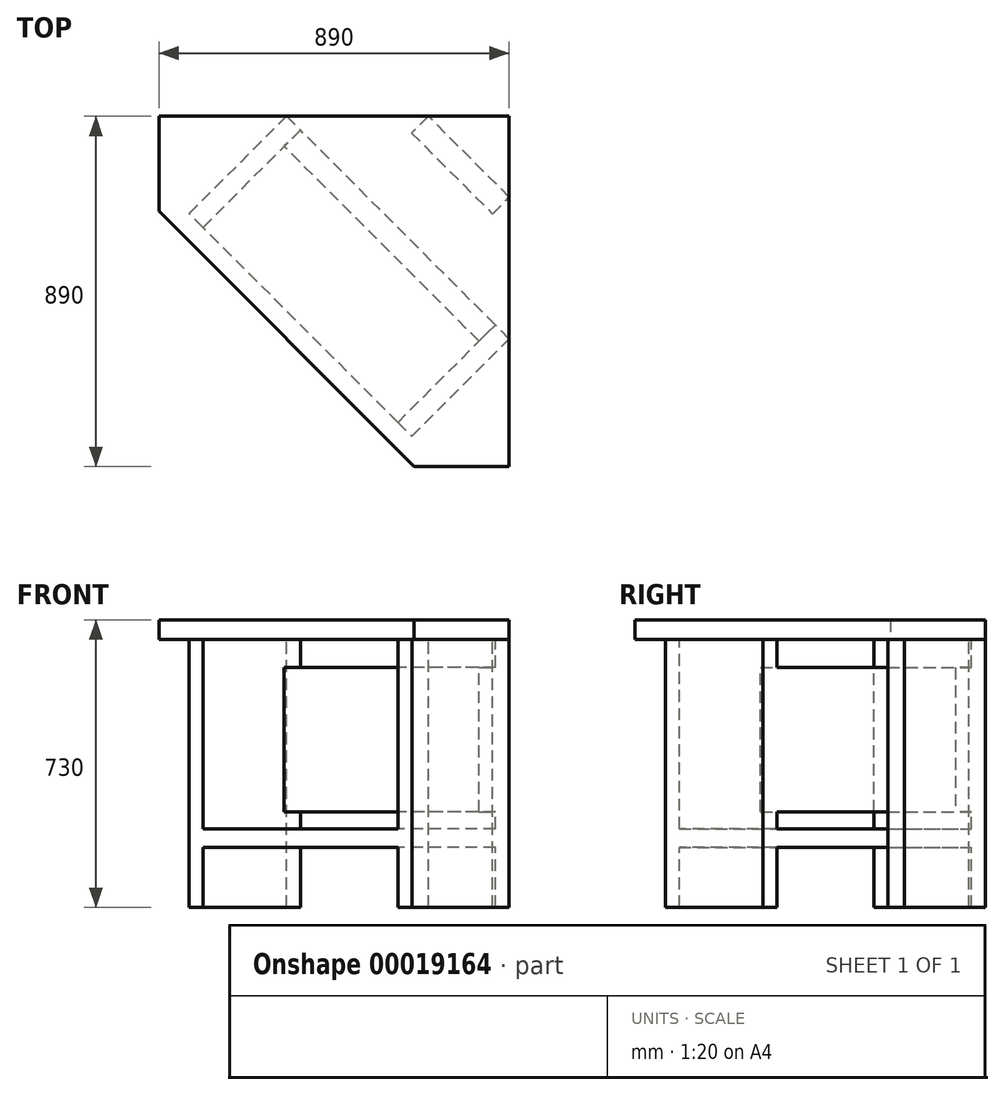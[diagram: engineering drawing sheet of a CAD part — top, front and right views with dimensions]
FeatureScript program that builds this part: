
annotation { "Feature Type Name" : "Feature", "Feature Type Description" : "" }
export const myFeature = defineFeature(function(context is Context, id is Id, definition is map)
    precondition{}
    {
        {
            var Q0;
            Q0=qCreatedBy(makeId("Top.planeOp"),FACE);
            var sketch = newSketch(context, id + "F0", { "sketchPlane" : qUnion([Q0])});
            skLineSegment(sketch, "E0", {"start": v(-890, 0) * mm, "end": v(0, 0) * mm});
            skLineSegment(sketch, "E1", {"start": v(0, 0) * mm, "end": v(0, -890) * mm});
            skLineSegment(sketch, "E2", {"start": v(0, -890) * mm, "end": v(-241.37, -890) * mm});
            skLineSegment(sketch, "E3", {"start": v(-241.37, -890) * mm, "end": v(-890, -241.37) * mm});
            skLineSegment(sketch, "E4", {"start": v(-890, -241.37) * mm, "end": v(-890, 0) * mm});
            skLineSegment(sketch, "E5", {"start": v(0, 0) * mm, "end": v(-565.69, -565.69) * mm, "construction": true});
            skSolve(sketch);
        }
        {
            var Q0;
            Q0=makeQuery(id+"F0.imprint","IMPRINT",FACE,{"disambiguationData":[TD([[makeQuery(id+"F0.imprint","IMPRINT",EDGE,{"derivedFrom":sQuery(id+"F0.wireOp",EDGE,"E0")}),-1.0]])]});
            extrude(context, id + "F1", {"entities" : qUnion([Q0]), "depth" : 50 * mm});
        }
        {
            var Q0;
            Q0=qCreatedBy(makeId("Right.planeOp"),FACE);
            var Q1;
            Q1=qCreatedBy(makeId("Front.planeOp"),FACE);
            cPlane(context, id + "F2", {"entities" : qUnion([Q0, Q1]), "cplaneType" : CPlaneType.MID_PLANE, "offset" : 150 * mm, "flipAlignment" : true, "width" : 150 * mm, "height" : 150 * mm});
        }
        {
            var Q0;
            Q0=qCreatedBy(makeId("Top.planeOp"),FACE);
            var sketch = newSketch(context, id + "F3", { "sketchPlane" : qUnion([Q0])});
            skLineSegment(sketch, "E6", {"start": v(-530.33, -35.36) * mm, "end": v(-777.82, -282.84) * mm});
            skLineSegment(sketch, "E7", {"start": v(-777.82, -282.84) * mm, "end": v(-813.17, -247.49) * mm});
            skLineSegment(sketch, "E8", {"start": v(-813.17, -247.49) * mm, "end": v(-565.69, 0) * mm});
            skLineSegment(sketch, "E9", {"start": v(-565.69, 0) * mm, "end": v(-530.33, -35.36) * mm});
            skLineSegment(sketch, "E10.MirrorCS", {"start": v(-35.36, -530.33) * mm, "end": v(-282.84, -777.82) * mm});
            skLineSegment(sketch, "E11.MirrorCS", {"start": v(-282.84, -777.82) * mm, "end": v(-247.49, -813.17) * mm});
            skLineSegment(sketch, "E12.MirrorCS", {"start": v(-247.49, -813.17) * mm, "end": v(0, -565.69) * mm});
            skLineSegment(sketch, "E13.MirrorCS", {"start": v(0, -565.69) * mm, "end": v(-35.36, -530.33) * mm});
            skLineSegment(sketch, "E14", {"start": v(0, -205.53) * mm, "end": v(-205.53, 0) * mm});
            skLineSegment(sketch, "E15", {"start": v(-205.53, 0) * mm, "end": v(-248.1, -42.57) * mm});
            skLineSegment(sketch, "E16", {"start": v(-248.1, -42.57) * mm, "end": v(-42.57, -248.1) * mm});
            skLineSegment(sketch, "E17", {"start": v(-42.57, -248.1) * mm, "end": v(0, -205.53) * mm});
            skPoint(sketch, "E18", {"position": v(-102.76, -102.76) * mm});
            skSolve(sketch);
        }
        {
            var Q0;
            Q0 = qSketchRegion(id + "F3", true);
            extrude(context, id + "F4", {"entities" : qUnion([Q0]), "operationType" : NewBodyOperationType.ADD, "oppositeDirection" : true, "depth" : 680 * mm});
        }
        {
            var Q0;
            Q0=makeQuery(id+"F4.opExtrude","SWEPT_FACE",FACE,{"disambiguationData":[OSD([sQuery(id+"F3.wireOp",EDGE,"E6")])]});
            var sketch = newSketch(context, id + "F5", { "sketchPlane" : qUnion([Q0])});
            skLineSegment(sketch, "E19.bottom", {"start": v(-750, -527.4) * mm, "end": v(-400, -527.4) * mm});
            skLineSegment(sketch, "E19.top", {"start": v(-750, -480.3) * mm, "end": v(-400, -480.3) * mm});
            skLineSegment(sketch, "E19.left", {"start": v(-750, -527.4) * mm, "end": v(-750, -480.3) * mm});
            skLineSegment(sketch, "E19.right", {"start": v(-400, -527.4) * mm, "end": v(-400, -480.3) * mm});
            skLineSegment(sketch, "E20.bottom", {"start": v(-400, -70.68) * mm, "end": v(-458.26, -70.68) * mm});
            skLineSegment(sketch, "E20.top", {"start": v(-400, -437.28) * mm, "end": v(-458.26, -437.28) * mm});
            skLineSegment(sketch, "E20.left", {"start": v(-400, -70.68) * mm, "end": v(-400, -437.28) * mm});
            skLineSegment(sketch, "E20.right", {"start": v(-458.26, -70.68) * mm, "end": v(-458.26, -437.28) * mm});
            skSolve(sketch);
        }
        {
            var Q0;
            Q0 = qSketchRegion(id + "F5", true);
            extrude(context, id + "F6", {"entities" : qUnion([Q0]), "operationType" : NewBodyOperationType.ADD, "endBound" : BoundingType.UP_TO_NEXT, "depth" : 25 * mm});
        }
    });
